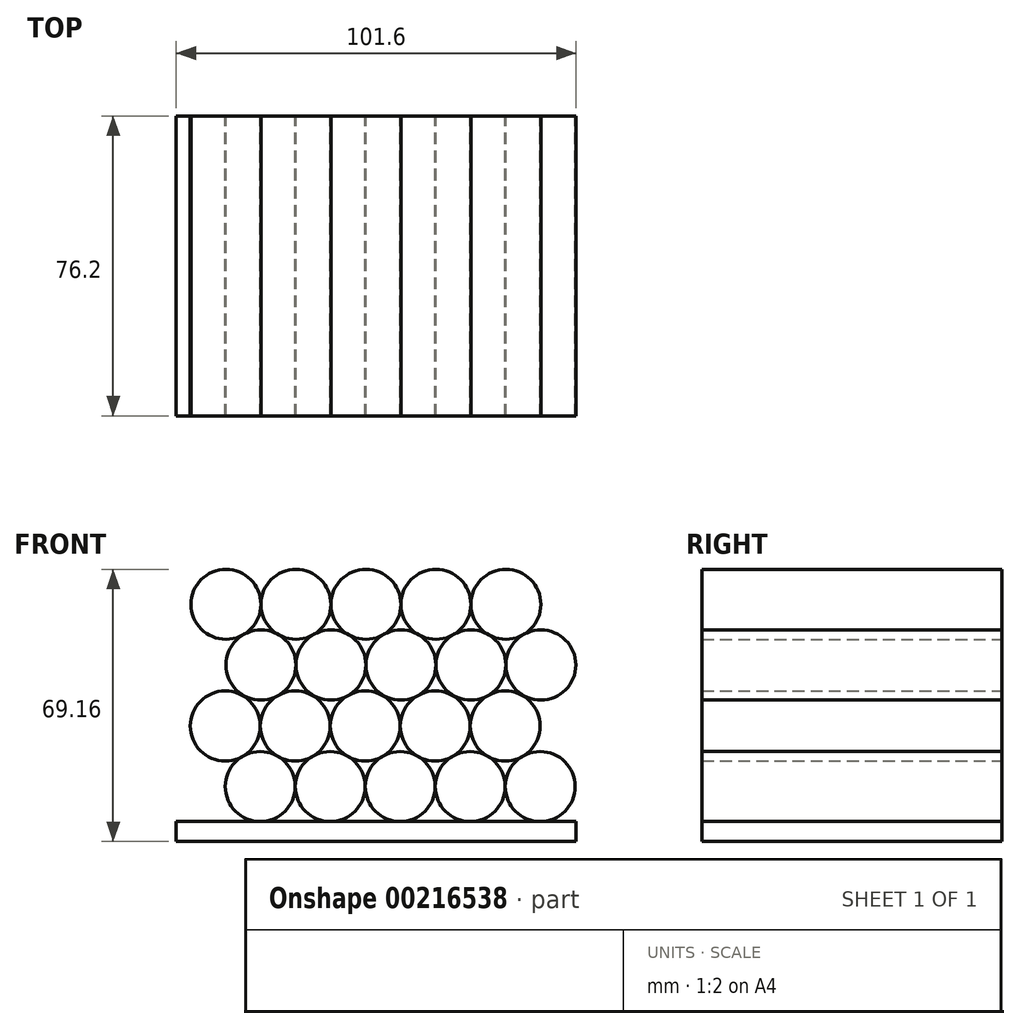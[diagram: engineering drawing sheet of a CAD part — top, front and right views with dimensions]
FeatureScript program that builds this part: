
annotation { "Feature Type Name" : "Feature", "Feature Type Description" : "" }
export const myFeature = defineFeature(function(context is Context, id is Id, definition is map)
    precondition{}
    {
        {
            var Q0;
            Q0=qCreatedBy(makeId("Front.planeOp"),FACE);
            var sketch = newSketch(context, id + "F0", { "sketchPlane" : qUnion([Q0])});
            skCircle(sketch, "E0", {"center": v(-29.45, -16.57) * mm, "radius": 8.9 * mm});
            skCircle(sketch, "E1", {"center": v(-11.67, -16.57) * mm, "radius": 8.9 * mm});
            skCircle(sketch, "E2", {"center": v(6.11, -16.57) * mm, "radius": 8.9 * mm});
            skCircle(sketch, "E3", {"center": v(23.9, -16.57) * mm, "radius": 8.9 * mm});
            skCircle(sketch, "E4", {"center": v(41.67, -16.57) * mm, "radius": 8.9 * mm});
            skLineSegment(sketch, "E5.bottom", {"start": v(-50.8, -25.46) * mm, "end": v(50.8, -25.46) * mm});
            skLineSegment(sketch, "E5.top", {"start": v(-50.8, -30.54) * mm, "end": v(50.8, -30.54) * mm});
            skLineSegment(sketch, "E5.left", {"start": v(-50.8, -25.46) * mm, "end": v(-50.8, -30.54) * mm});
            skLineSegment(sketch, "E5.right", {"start": v(50.8, -25.46) * mm, "end": v(50.8, -30.54) * mm});
            skCircle(sketch, "E6", {"center": v(-38.34, -1.17) * mm, "radius": 8.9 * mm});
            skCircle(sketch, "E7", {"center": v(-20.56, -1.17) * mm, "radius": 8.9 * mm});
            skCircle(sketch, "E8", {"center": v(-2.78, -1.17) * mm, "radius": 8.9 * mm});
            skCircle(sketch, "E9", {"center": v(15, -1.17) * mm, "radius": 8.9 * mm});
            skCircle(sketch, "E10", {"center": v(32.78, -1.17) * mm, "radius": 8.9 * mm});
            skCircle(sketch, "E11", {"center": v(-29.26, 14.34) * mm, "radius": 8.9 * mm});
            skCircle(sketch, "E12", {"center": v(-11.48, 14.34) * mm, "radius": 8.9 * mm});
            skCircle(sketch, "E13", {"center": v(6.3, 14.34) * mm, "radius": 8.9 * mm});
            skCircle(sketch, "E14", {"center": v(24.08, 14.34) * mm, "radius": 8.9 * mm});
            skCircle(sketch, "E15", {"center": v(41.86, 14.34) * mm, "radius": 8.9 * mm});
            skCircle(sketch, "E16", {"center": v(-38.15, 29.73) * mm, "radius": 8.9 * mm});
            skCircle(sketch, "E17", {"center": v(-20.37, 29.73) * mm, "radius": 8.9 * mm});
            skCircle(sketch, "E18", {"center": v(-2.6, 29.73) * mm, "radius": 8.9 * mm});
            skCircle(sketch, "E19", {"center": v(15.19, 29.73) * mm, "radius": 8.9 * mm});
            skCircle(sketch, "E20", {"center": v(32.97, 29.73) * mm, "radius": 8.9 * mm});
            skSolve(sketch);
        }
        {
            var Q0;
            {var subQ0=sQuery(id+"F0.wireOp",EDGE,"0c1801c8-23d2-4a07-8585-4b4ae403161c");var subQ1=makeQuery(id+"F0.imprint","INTERSECT",VERTEX,{"derivedFrom":[sQuery(id+"F0.wireOp",EDGE,"f0896b75-7ff4-490b-9eb5-08945ea8ef80"),subQ0]});Q0=makeQuery(id+"F0.imprint","IMPRINT",FACE,{"disambiguationData":[TD([[makeQuery(id+"F0.imprint","IMPRINT",EDGE,{"disambiguationData":[TD([[subQ1,1.0]])],"derivedFrom":subQ0}),1.0]])]});}
            var Q1;
            {var subQ0=sQuery(id+"F0.wireOp",EDGE,"5af625b9-71d9-4944-9748-d1b5f725a47c");var subQ1=makeQuery(id+"F0.imprint","INTERSECT",VERTEX,{"derivedFrom":[sQuery(id+"F0.wireOp",EDGE,"0c1801c8-23d2-4a07-8585-4b4ae403161c"),subQ0]});Q1=makeQuery(id+"F0.imprint","IMPRINT",FACE,{"disambiguationData":[TD([[makeQuery(id+"F0.imprint","IMPRINT",EDGE,{"disambiguationData":[TD([[subQ1,1.0]])],"derivedFrom":subQ0}),1.0]])]});}
            var Q2;
            {var subQ0=sQuery(id+"F0.wireOp",EDGE,"cf587e86-f61d-495c-ab6c-7963b9340b9b");var subQ1=makeQuery(id+"F0.imprint","INTERSECT",VERTEX,{"derivedFrom":[sQuery(id+"F0.wireOp",EDGE,"5af625b9-71d9-4944-9748-d1b5f725a47c"),subQ0]});Q2=makeQuery(id+"F0.imprint","IMPRINT",FACE,{"disambiguationData":[TD([[makeQuery(id+"F0.imprint","IMPRINT",EDGE,{"disambiguationData":[TD([[subQ1,-1.0]])],"derivedFrom":subQ0}),1.0]])]});}
            var Q3;
            {var subQ0=sQuery(id+"F0.wireOp",EDGE,"6513f72b-f417-4675-a262-e46438cbcac2");var subQ1=makeQuery(id+"F0.imprint","INTERSECT",VERTEX,{"derivedFrom":[subQ0,sQuery(id+"F0.wireOp",EDGE,"cf587e86-f61d-495c-ab6c-7963b9340b9b")]});Q3=makeQuery(id+"F0.imprint","IMPRINT",FACE,{"disambiguationData":[TD([[makeQuery(id+"F0.imprint","IMPRINT",EDGE,{"disambiguationData":[TD([[subQ1,-1.0]])],"derivedFrom":subQ0}),1.0]])]});}
            var Q4;
            {var subQ0=sQuery(id+"F0.wireOp",EDGE,"b3fe10dc-f5bd-422b-85db-0323ad2a796b");var subQ4=makeQuery(id+"F0.imprint","INTERSECT",VERTEX,{"derivedFrom":[subQ0,sQuery(id+"F0.wireOp",EDGE,"cf587e86-f61d-495c-ab6c-7963b9340b9b")]});Q4=makeQuery(id+"F0.imprint","IMPRINT",FACE,{"disambiguationData":[TD([[makeQuery(id+"F0.imprint","IMPRINT",EDGE,{"disambiguationData":[TD([[subQ4,1.0]])],"derivedFrom":subQ0}),1.0]])]});}
            var Q5;
            {var subQ0=sQuery(id+"F0.wireOp",EDGE,"20095c58-7453-4e6b-84d0-4050fc440cec");var subQ4=makeQuery(id+"F0.imprint","INTERSECT",VERTEX,{"derivedFrom":[subQ0,sQuery(id+"F0.wireOp",EDGE,"5af625b9-71d9-4944-9748-d1b5f725a47c")]});Q5=makeQuery(id+"F0.imprint","IMPRINT",FACE,{"disambiguationData":[TD([[makeQuery(id+"F0.imprint","IMPRINT",EDGE,{"disambiguationData":[TD([[subQ4,1.0]])],"derivedFrom":subQ0}),1.0]])]});}
            var Q6;
            {var subQ0=sQuery(id+"F0.wireOp",EDGE,"f0896b75-7ff4-490b-9eb5-08945ea8ef80");var subQ1=makeQuery(id+"F0.imprint","INTERSECT",VERTEX,{"derivedFrom":[subQ0,sQuery(id+"F0.wireOp",EDGE,"0c1801c8-23d2-4a07-8585-4b4ae403161c")]});Q6=makeQuery(id+"F0.imprint","IMPRINT",FACE,{"disambiguationData":[TD([[makeQuery(id+"F0.imprint","IMPRINT",EDGE,{"disambiguationData":[TD([[subQ1,1.0]])],"derivedFrom":subQ0}),1.0]])]});}
            var Q7;
            {var subQ0=sQuery(id+"F0.wireOp",EDGE,"E0");var subQ1=makeQuery(id+"F0.imprint","INTERSECT",VERTEX,{"derivedFrom":[sQuery(id+"F0.wireOp",EDGE,"f0896b75-7ff4-490b-9eb5-08945ea8ef80"),subQ0]});Q7=makeQuery(id+"F0.imprint","IMPRINT",FACE,{"disambiguationData":[TD([[makeQuery(id+"F0.imprint","IMPRINT",EDGE,{"disambiguationData":[TD([[subQ1,1.0]])],"derivedFrom":subQ0}),1.0]])]});}
            var Q8;
            {var subQ0=sQuery(id+"F0.wireOp",EDGE,"E1");var subQ4=makeQuery(id+"F0.imprint","INTERSECT",VERTEX,{"derivedFrom":[sQuery(id+"F0.wireOp",EDGE,"20095c58-7453-4e6b-84d0-4050fc440cec"),subQ0]});Q8=makeQuery(id+"F0.imprint","IMPRINT",FACE,{"disambiguationData":[TD([[makeQuery(id+"F0.imprint","IMPRINT",EDGE,{"disambiguationData":[TD([[subQ4,1.0]])],"derivedFrom":subQ0}),1.0]])]});}
            var Q9;
            {var subQ0=sQuery(id+"F0.wireOp",EDGE,"E2");var subQ4=makeQuery(id+"F0.imprint","INTERSECT",VERTEX,{"derivedFrom":[sQuery(id+"F0.wireOp",EDGE,"b3fe10dc-f5bd-422b-85db-0323ad2a796b"),subQ0]});Q9=makeQuery(id+"F0.imprint","IMPRINT",FACE,{"disambiguationData":[TD([[makeQuery(id+"F0.imprint","IMPRINT",EDGE,{"disambiguationData":[TD([[subQ4,1.0]])],"derivedFrom":subQ0}),1.0]])]});}
            var Q10;
            {var subQ0=sQuery(id+"F0.wireOp",EDGE,"E3");var subQ4=makeQuery(id+"F0.imprint","INTERSECT",VERTEX,{"derivedFrom":[sQuery(id+"F0.wireOp",EDGE,"6513f72b-f417-4675-a262-e46438cbcac2"),subQ0]});Q10=makeQuery(id+"F0.imprint","IMPRINT",FACE,{"disambiguationData":[TD([[makeQuery(id+"F0.imprint","IMPRINT",EDGE,{"disambiguationData":[TD([[subQ4,1.0]])],"derivedFrom":subQ0}),1.0]])]});}
            var Q11;
            {var subQ0=sQuery(id+"F0.wireOp",EDGE,"E4");var subQ1=makeQuery(id+"F0.imprint","INTERSECT",VERTEX,{"derivedFrom":[sQuery(id+"F0.wireOp",EDGE,"6513f72b-f417-4675-a262-e46438cbcac2"),subQ0]});Q11=makeQuery(id+"F0.imprint","IMPRINT",FACE,{"disambiguationData":[TD([[makeQuery(id+"F0.imprint","IMPRINT",EDGE,{"disambiguationData":[TD([[subQ1,-1.0]])],"derivedFrom":subQ0}),1.0]])]});}
            var Q12;
            Q12=makeQuery(id+"F0.imprint","IMPRINT",FACE,{"disambiguationData":[TD([[makeQuery(id+"F0.imprint","IMPRINT",EDGE,{"derivedFrom":sQuery(id+"F0.wireOp",EDGE,"E5.top")}),1.0]])]});
            var Q13;
            {var subQ0=sQuery(id+"F0.wireOp",EDGE,"b7209964-fce2-4c74-a03b-dcfcf9720273");var subQ1=makeQuery(id+"F0.imprint","INTERSECT",VERTEX,{"derivedFrom":[subQ0,sQuery(id+"F0.wireOp",EDGE,"826bc404-7e04-4ebb-a8bb-261f92a73414")]});Q13=makeQuery(id+"F0.imprint","IMPRINT",FACE,{"disambiguationData":[TD([[makeQuery(id+"F0.imprint","IMPRINT",EDGE,{"disambiguationData":[TD([[subQ1,1.0]])],"derivedFrom":subQ0}),1.0]])]});}
            var Q14;
            {var subQ0=sQuery(id+"F0.wireOp",EDGE,"4bfdec23-dac0-4773-80be-c3509125d457");var subQ1=makeQuery(id+"F0.imprint","INTERSECT",VERTEX,{"derivedFrom":[subQ0,sQuery(id+"F0.wireOp",EDGE,"826bc404-7e04-4ebb-a8bb-261f92a73414")]});Q14=makeQuery(id+"F0.imprint","IMPRINT",FACE,{"disambiguationData":[TD([[makeQuery(id+"F0.imprint","IMPRINT",EDGE,{"disambiguationData":[TD([[subQ1,-1.0]])],"derivedFrom":subQ0}),1.0]])]});}
            var Q15;
            {var subQ0=sQuery(id+"F0.wireOp",EDGE,"826bc404-7e04-4ebb-a8bb-261f92a73414");var subQ1=makeQuery(id+"F0.imprint","INTERSECT",VERTEX,{"derivedFrom":[sQuery(id+"F0.wireOp",EDGE,"b7209964-fce2-4c74-a03b-dcfcf9720273"),subQ0]});Q15=makeQuery(id+"F0.imprint","IMPRINT",FACE,{"disambiguationData":[TD([[makeQuery(id+"F0.imprint","IMPRINT",EDGE,{"disambiguationData":[TD([[subQ1,-1.0]])],"derivedFrom":subQ0}),1.0]])]});}
            var Q16;
            {var subQ0=sQuery(id+"F0.wireOp",EDGE,"E6");var subQ1=makeQuery(id+"F0.imprint","INTERSECT",VERTEX,{"derivedFrom":[sQuery(id+"F0.wireOp",EDGE,"E0"),subQ0]});Q16=makeQuery(id+"F0.imprint","IMPRINT",FACE,{"disambiguationData":[TD([[makeQuery(id+"F0.imprint","IMPRINT",EDGE,{"disambiguationData":[TD([[subQ1,1.0]])],"derivedFrom":subQ0}),1.0]])]});}
            var Q17;
            {var subQ0=sQuery(id+"F0.wireOp",EDGE,"E7");var subQ4=makeQuery(id+"F0.imprint","INTERSECT",VERTEX,{"derivedFrom":[subQ0,sQuery(id+"F0.wireOp",EDGE,"E11")]});Q17=makeQuery(id+"F0.imprint","IMPRINT",FACE,{"disambiguationData":[TD([[makeQuery(id+"F0.imprint","IMPRINT",EDGE,{"disambiguationData":[TD([[subQ4,1.0]])],"derivedFrom":subQ0}),1.0]])]});}
            var Q18;
            {var subQ0=sQuery(id+"F0.wireOp",EDGE,"E8");var subQ4=makeQuery(id+"F0.imprint","INTERSECT",VERTEX,{"derivedFrom":[subQ0,sQuery(id+"F0.wireOp",EDGE,"E12")]});Q18=makeQuery(id+"F0.imprint","IMPRINT",FACE,{"disambiguationData":[TD([[makeQuery(id+"F0.imprint","IMPRINT",EDGE,{"disambiguationData":[TD([[subQ4,1.0]])],"derivedFrom":subQ0}),1.0]])]});}
            var Q19;
            {var subQ0=sQuery(id+"F0.wireOp",EDGE,"E9");var subQ4=makeQuery(id+"F0.imprint","INTERSECT",VERTEX,{"derivedFrom":[subQ0,sQuery(id+"F0.wireOp",EDGE,"E13")]});Q19=makeQuery(id+"F0.imprint","IMPRINT",FACE,{"disambiguationData":[TD([[makeQuery(id+"F0.imprint","IMPRINT",EDGE,{"disambiguationData":[TD([[subQ4,1.0]])],"derivedFrom":subQ0}),1.0]])]});}
            var Q20;
            {var subQ0=sQuery(id+"F0.wireOp",EDGE,"E10");var subQ1=makeQuery(id+"F0.imprint","INTERSECT",VERTEX,{"derivedFrom":[subQ0,sQuery(id+"F0.wireOp",EDGE,"E14")]});Q20=makeQuery(id+"F0.imprint","IMPRINT",FACE,{"disambiguationData":[TD([[makeQuery(id+"F0.imprint","IMPRINT",EDGE,{"disambiguationData":[TD([[subQ1,-1.0]])],"derivedFrom":subQ0}),1.0]])]});}
            var Q21;
            {var subQ0=sQuery(id+"F0.wireOp",EDGE,"E15");var subQ1=makeQuery(id+"F0.imprint","INTERSECT",VERTEX,{"derivedFrom":[sQuery(id+"F0.wireOp",EDGE,"E14"),subQ0]});Q21=makeQuery(id+"F0.imprint","IMPRINT",FACE,{"disambiguationData":[TD([[makeQuery(id+"F0.imprint","IMPRINT",EDGE,{"disambiguationData":[TD([[subQ1,1.0]])],"derivedFrom":subQ0}),1.0]])]});}
            var Q22;
            {var subQ0=sQuery(id+"F0.wireOp",EDGE,"E14");var subQ5=makeQuery(id+"F0.imprint","INTERSECT",VERTEX,{"derivedFrom":[subQ0,sQuery(id+"F0.wireOp",EDGE,"E15")]});Q22=makeQuery(id+"F0.imprint","IMPRINT",FACE,{"disambiguationData":[TD([[makeQuery(id+"F0.imprint","IMPRINT",EDGE,{"disambiguationData":[TD([[subQ5,-1.0]])],"derivedFrom":subQ0}),1.0]])]});}
            var Q23;
            {var subQ0=sQuery(id+"F0.wireOp",EDGE,"E13");var subQ4=makeQuery(id+"F0.imprint","INTERSECT",VERTEX,{"derivedFrom":[subQ0,sQuery(id+"F0.wireOp",EDGE,"E19")]});Q23=makeQuery(id+"F0.imprint","IMPRINT",FACE,{"disambiguationData":[TD([[makeQuery(id+"F0.imprint","IMPRINT",EDGE,{"disambiguationData":[TD([[subQ4,1.0]])],"derivedFrom":subQ0}),1.0]])]});}
            var Q24;
            {var subQ0=sQuery(id+"F0.wireOp",EDGE,"E12");var subQ4=makeQuery(id+"F0.imprint","INTERSECT",VERTEX,{"derivedFrom":[subQ0,sQuery(id+"F0.wireOp",EDGE,"E18")]});Q24=makeQuery(id+"F0.imprint","IMPRINT",FACE,{"disambiguationData":[TD([[makeQuery(id+"F0.imprint","IMPRINT",EDGE,{"disambiguationData":[TD([[subQ4,1.0]])],"derivedFrom":subQ0}),1.0]])]});}
            var Q25;
            {var subQ0=sQuery(id+"F0.wireOp",EDGE,"E11");var subQ1=makeQuery(id+"F0.imprint","INTERSECT",VERTEX,{"derivedFrom":[subQ0,sQuery(id+"F0.wireOp",EDGE,"E17")]});Q25=makeQuery(id+"F0.imprint","IMPRINT",FACE,{"disambiguationData":[TD([[makeQuery(id+"F0.imprint","IMPRINT",EDGE,{"disambiguationData":[TD([[subQ1,1.0]])],"derivedFrom":subQ0}),1.0]])]});}
            var Q26;
            {var subQ0=sQuery(id+"F0.wireOp",EDGE,"E16");var subQ1=makeQuery(id+"F0.imprint","INTERSECT",VERTEX,{"derivedFrom":[sQuery(id+"F0.wireOp",EDGE,"E11"),subQ0]});Q26=makeQuery(id+"F0.imprint","IMPRINT",FACE,{"disambiguationData":[TD([[makeQuery(id+"F0.imprint","IMPRINT",EDGE,{"disambiguationData":[TD([[subQ1,1.0]])],"derivedFrom":subQ0}),1.0]])]});}
            var Q27;
            {var subQ0=sQuery(id+"F0.wireOp",EDGE,"E17");var subQ1=makeQuery(id+"F0.imprint","INTERSECT",VERTEX,{"derivedFrom":[sQuery(id+"F0.wireOp",EDGE,"E16"),subQ0]});Q27=makeQuery(id+"F0.imprint","IMPRINT",FACE,{"disambiguationData":[TD([[makeQuery(id+"F0.imprint","IMPRINT",EDGE,{"disambiguationData":[TD([[subQ1,1.0]])],"derivedFrom":subQ0}),1.0]])]});}
            var Q28;
            {var subQ0=sQuery(id+"F0.wireOp",EDGE,"E18");var subQ1=makeQuery(id+"F0.imprint","INTERSECT",VERTEX,{"derivedFrom":[sQuery(id+"F0.wireOp",EDGE,"E17"),subQ0]});Q28=makeQuery(id+"F0.imprint","IMPRINT",FACE,{"disambiguationData":[TD([[makeQuery(id+"F0.imprint","IMPRINT",EDGE,{"disambiguationData":[TD([[subQ1,1.0]])],"derivedFrom":subQ0}),1.0]])]});}
            var Q29;
            {var subQ0=sQuery(id+"F0.wireOp",EDGE,"E19");var subQ1=makeQuery(id+"F0.imprint","INTERSECT",VERTEX,{"derivedFrom":[sQuery(id+"F0.wireOp",EDGE,"E18"),subQ0]});Q29=makeQuery(id+"F0.imprint","IMPRINT",FACE,{"disambiguationData":[TD([[makeQuery(id+"F0.imprint","IMPRINT",EDGE,{"disambiguationData":[TD([[subQ1,1.0]])],"derivedFrom":subQ0}),1.0]])]});}
            var Q30;
            {var subQ0=sQuery(id+"F0.wireOp",EDGE,"E20");var subQ1=makeQuery(id+"F0.imprint","INTERSECT",VERTEX,{"derivedFrom":[sQuery(id+"F0.wireOp",EDGE,"E19"),subQ0]});Q30=makeQuery(id+"F0.imprint","IMPRINT",FACE,{"disambiguationData":[TD([[makeQuery(id+"F0.imprint","IMPRINT",EDGE,{"disambiguationData":[TD([[subQ1,-1.0]])],"derivedFrom":subQ0}),1.0]])]});}
            var Q31;
            Q31=sQuery(id+"F0.wireOp",EDGE,"5af625b9-71d9-4944-9748-d1b5f725a47c");
            var Q32;
            Q32=sQuery(id+"F0.wireOp",EDGE,"cf587e86-f61d-495c-ab6c-7963b9340b9b");
            var Q33;
            Q33=sQuery(id+"F0.wireOp",EDGE,"E5.bottom");
            var Q34;
            Q34=sQuery(id+"F0.wireOp",EDGE,"20095c58-7453-4e6b-84d0-4050fc440cec");
            var Q35;
            Q35=sQuery(id+"F0.wireOp",EDGE,"6513f72b-f417-4675-a262-e46438cbcac2");
            var Q36;
            Q36=sQuery(id+"F0.wireOp",EDGE,"0c1801c8-23d2-4a07-8585-4b4ae403161c");
            var Q37;
            Q37=sQuery(id+"F0.wireOp",EDGE,"E4");
            var Q38;
            Q38=sQuery(id+"F0.wireOp",EDGE,"E1");
            var Q39;
            Q39=sQuery(id+"F0.wireOp",EDGE,"b3fe10dc-f5bd-422b-85db-0323ad2a796b");
            var Q40;
            Q40=sQuery(id+"F0.wireOp",EDGE,"E5.top");
            var Q41;
            Q41=sQuery(id+"F0.wireOp",EDGE,"f0896b75-7ff4-490b-9eb5-08945ea8ef80");
            var Q42;
            Q42=sQuery(id+"F0.wireOp",EDGE,"E2");
            var Q43;
            Q43=sQuery(id+"F0.wireOp",EDGE,"E3");
            var Q44;
            Q44=sQuery(id+"F0.wireOp",EDGE,"E0");
            var Q45;
            Q45=sQuery(id+"F0.wireOp",EDGE,"E5.left");
            var Q46;
            Q46=sQuery(id+"F0.wireOp",EDGE,"E5.right");
            extrude(context, id + "F1", {"entities" : qUnion([Q0, Q1, Q2, Q3, Q4, Q5, Q6, Q7, Q8, Q9, Q10, Q11, Q12, Q13, Q14, Q15, Q16, Q17, Q18, Q19, Q20, Q21, Q22, Q23, Q24, Q25, Q26, Q27, Q28, Q29, Q30]), "surfaceEntities" : qUnion([Q31, Q32, Q33, Q34, Q35, Q36, Q37, Q38, Q39, Q40, Q41, Q42, Q43, Q44, Q45, Q46]), "depth" : 76.2 * mm});
        }
    });
